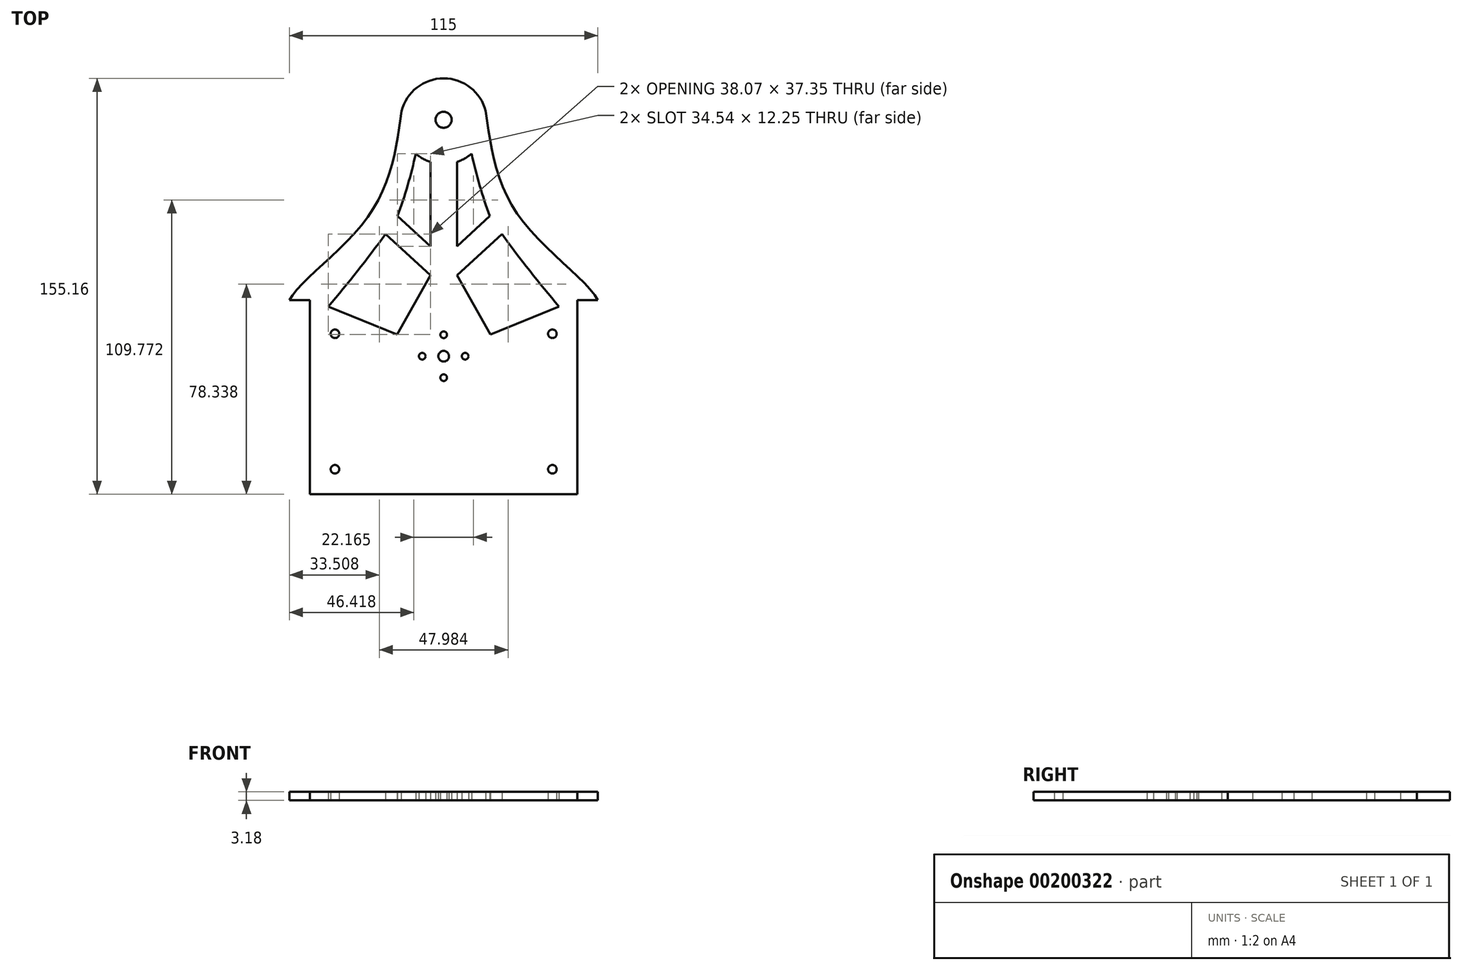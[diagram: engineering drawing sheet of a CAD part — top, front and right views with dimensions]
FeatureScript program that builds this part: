
annotation { "Feature Type Name" : "Feature", "Feature Type Description" : "" }
export const myFeature = defineFeature(function(context is Context, id is Id, definition is map)
    precondition{}
    {
        {
            var Q0;
            Q0=qCreatedBy(makeId("Top.planeOp"),FACE);
            var sketch = newSketch(context, id + "F0", { "sketchPlane" : qUnion([Q0])});
            skPoint(sketch, "E0.middle", {"position": v(0, 0) * mm});
            skPoint(sketch, "E1.orphan", {"position": v(-101.6, 120.65) * mm});
            skPoint(sketch, "E2.orphan", {"position": v(101.6, 120.65) * mm});
            skPoint(sketch, "E3.middle", {"position": v(0, -44.45) * mm});
            skPoint(sketch, "E4.middle", {"position": v(-64.58, -39.48) * mm});
            skPoint(sketch, "E5.orphan", {"position": v(-88.9, 0) * mm});
            skLineSegment(sketch, "E6", {"start": v(-49.88, -63.5) * mm, "end": v(49.88, -63.5) * mm});
            skLineSegment(sketch, "E7", {"start": v(-57.5, 8.9) * mm, "end": v(-49.88, 8.9) * mm});
            skLineSegment(sketch, "E8", {"start": v(-49.88, 8.9) * mm, "end": v(-49.88, -63.5) * mm});
            skPoint(sketch, "E9.orphan", {"position": v(-51.88, -63.5) * mm});
            skLineSegment(sketch, "E10.MirrorCS", {"start": v(49.88, 8.9) * mm, "end": v(49.88, -63.5) * mm});
            skLineSegment(sketch, "E11.MirrorCS", {"start": v(57.5, 8.9) * mm, "end": v(49.88, 8.9) * mm});
            skLineSegment(sketch, "E12.bottom", {"start": v(-50.88, 5.52) * mm, "end": v(-69.93, 5.52) * mm, "construction": true});
            skLineSegment(sketch, "E12.top", {"start": v(-50.88, -57.98) * mm, "end": v(-69.93, -57.98) * mm, "construction": true});
            skLineSegment(sketch, "E12.left", {"start": v(-50.88, 5.52) * mm, "end": v(-50.88, -57.98) * mm, "construction": true});
            skLineSegment(sketch, "E12.right", {"start": v(-69.93, 5.52) * mm, "end": v(-69.93, -57.98) * mm, "construction": true});
            skLineSegment(sketch, "E13.MirrorCS", {"start": v(50.88, 5.52) * mm, "end": v(69.93, 5.52) * mm, "construction": true});
            skLineSegment(sketch, "E14.MirrorCS", {"start": v(50.88, 5.52) * mm, "end": v(50.88, -57.98) * mm, "construction": true});
            skLineSegment(sketch, "E15.MirrorCS", {"start": v(50.88, -57.98) * mm, "end": v(69.93, -57.98) * mm, "construction": true});
            skLineSegment(sketch, "E16.MirrorCS", {"start": v(69.93, 5.52) * mm, "end": v(69.93, -57.98) * mm, "construction": true});
            skCircle(sketch, "E17", {"center": v(-0.03, 76.2) * mm, "radius": 3 * mm});
            skCircle(sketch, "E18", {"center": v(-0.03, 76.2) * mm, "radius": 63.5 * mm, "construction": true});
            skFitSpline(sketch, "E19", {"points": [v(-15.7, 79.38) * mm, v(-28.38, 39.82) * mm, v(-57.5, 8.9) * mm, v(-57.5, 1.27) * mm], "startDerivative": vector(-13.48, -99.48) * mm, "endDerivative": vector(13.07, -39.2) * mm});
            skFitSpline(sketch, "E20.MirrorCS", {"points": [v(15.7, 79.38) * mm, v(28.38, 39.82) * mm, v(57.5, 8.9) * mm, v(57.5, 1.27) * mm], "startDerivative": vector(13.48, -99.48) * mm, "endDerivative": vector(-13.07, -39.2) * mm});
            skArc(sketch, "E21", {"start": v(15.7, 79.38) * mm, "mid": v(0, 91.66) * mm, "end": v(-15.7, 79.38) * mm});
            skArc(sketch, "E22", {"start": v(-15.7, 79.38) * mm, "mid": v(-15.96, 78) * mm, "end": v(-16.09, 76.6) * mm});
            skLineSegment(sketch, "E23", {"start": v(-4.96, 60.5) * mm, "end": v(-4.96, 29) * mm});
            skLineSegment(sketch, "E24", {"start": v(-4.96, 29) * mm, "end": v(-17.2, 40.24) * mm});
            skArc(sketch, "E25", {"start": v(-17.2, 40.24) * mm, "mid": v(-13.4, 51.77) * mm, "end": v(-10.42, 63.54) * mm});
            skLineSegment(sketch, "E26", {"start": v(-4.96, 18.14) * mm, "end": v(-17.38, -3.84) * mm});
            skLineSegment(sketch, "E27", {"start": v(-17.38, -3.84) * mm, "end": v(-43.03, 6.52) * mm});
            skLineSegment(sketch, "E28", {"start": v(-4.96, 18.14) * mm, "end": v(-21.7, 33.51) * mm});
            skArc(sketch, "E29", {"start": v(-43.03, 6.52) * mm, "mid": v(-32.1, 19.81) * mm, "end": v(-21.7, 33.51) * mm});
            skLineSegment(sketch, "E30.MirrorCS", {"start": v(4.96, 18.14) * mm, "end": v(17.38, -3.84) * mm});
            skLineSegment(sketch, "E31.MirrorCS", {"start": v(4.96, 18.14) * mm, "end": v(21.7, 33.51) * mm});
            skLineSegment(sketch, "E32.MirrorCS", {"start": v(4.96, 29) * mm, "end": v(17.2, 40.24) * mm});
            skArc(sketch, "E33.MirrorCS", {"start": v(17.2, 40.24) * mm, "mid": v(13.4, 51.77) * mm, "end": v(10.42, 63.54) * mm});
            skLineSegment(sketch, "E34.MirrorCS", {"start": v(4.96, 60.5) * mm, "end": v(4.96, 29) * mm});
            skArc(sketch, "E35.MirrorCS", {"start": v(43.03, 6.52) * mm, "mid": v(32.1, 19.81) * mm, "end": v(21.7, 33.51) * mm});
            skLineSegment(sketch, "E36.MirrorCS", {"start": v(17.38, -3.84) * mm, "end": v(43.03, 6.52) * mm});
            skArc(sketch, "E37.trimOffspring", {"start": v(4.96, 60.5) * mm, "mid": v(7.84, 61.75) * mm, "end": v(10.42, 63.54) * mm});
            skLineSegment(sketch, "E38.trimOffspring", {"start": v(15.7, 79.38) * mm, "end": v(15.7, 79.38) * mm});
            skArc(sketch, "E39.trimOffspring", {"start": v(-10.42, 63.54) * mm, "mid": v(-7.84, 61.75) * mm, "end": v(-4.96, 60.5) * mm});
            skLineSegment(sketch, "E40.bottom", {"start": v(-49.88, -63.5) * mm, "end": v(-40.53, -63.5) * mm, "construction": true});
            skLineSegment(sketch, "E40.top", {"start": v(-49.88, -54.15) * mm, "end": v(-40.53, -54.15) * mm, "construction": true});
            skLineSegment(sketch, "E40.left", {"start": v(-49.88, -63.5) * mm, "end": v(-49.88, -54.15) * mm, "construction": true});
            skLineSegment(sketch, "E40.right", {"start": v(-40.53, -63.5) * mm, "end": v(-40.53, -54.15) * mm, "construction": true});
            skCircle(sketch, "E41", {"center": v(-40.53, -54.15) * mm, "radius": 1.6 * mm});
            skLineSegment(sketch, "E42.bottom", {"start": v(-49.88, 8.9) * mm, "end": v(-40.53, 8.9) * mm, "construction": true});
            skLineSegment(sketch, "E42.top", {"start": v(-49.88, -3.63) * mm, "end": v(-40.53, -3.63) * mm, "construction": true});
            skLineSegment(sketch, "E42.left", {"start": v(-49.88, 8.9) * mm, "end": v(-49.88, -3.63) * mm, "construction": true});
            skLineSegment(sketch, "E42.right", {"start": v(-40.53, 8.9) * mm, "end": v(-40.53, -3.63) * mm, "construction": true});
            skCircle(sketch, "E43", {"center": v(-40.53, -3.63) * mm, "radius": 1.6 * mm});
            skCircle(sketch, "E44.MirrorC", {"center": v(40.53, -3.63) * mm, "radius": 1.6 * mm});
            skCircle(sketch, "E45.MirrorC", {"center": v(40.53, -54.15) * mm, "radius": 1.6 * mm});
            skCircle(sketch, "E46", {"center": v(0, -12) * mm, "radius": 13.5 * mm, "construction": true});
            skCircle(sketch, "E47", {"center": v(0, -12) * mm, "radius": 2 * mm});
            skCircle(sketch, "E48", {"center": v(0, -4) * mm, "radius": 1.25 * mm});
            skLineSegment(sketch, "E49", {"start": v(-13.5, -12) * mm, "end": v(13.5, -12) * mm, "construction": true});
            skCircle(sketch, "E50.1.0", {"center": v(-8, -12) * mm, "radius": 1.25 * mm});
            skCircle(sketch, "E50.2.0", {"center": v(0, -20) * mm, "radius": 1.25 * mm});
            skCircle(sketch, "E50.3.0", {"center": v(8, -12) * mm, "radius": 1.25 * mm});
            skSolve(sketch);
        }
        {
            var Q0;
            Q0=makeQuery(id+"F0.imprint","IMPRINT",FACE,{"disambiguationData":[TD([[makeQuery(id+"F0.imprint","IMPRINT",EDGE,{"derivedFrom":sQuery(id+"F0.wireOp",EDGE,"XoACZhgm-4fXt-D90R-Zf98-5iFfzIu4IJjn")}),1.0]])]});
            var Q1;
            Q1=makeQuery(id+"F0.imprint","IMPRINT",FACE,{"disambiguationData":[TD([[makeQuery(id+"F0.imprint","IMPRINT",EDGE,{"derivedFrom":sQuery(id+"F0.wireOp",EDGE,"E3.bottom")}),1.0]])]});
            var Q2;
            {var subQ3=sQuery(id+"F0.wireOp",EDGE,"6qRwDFxo-6jyo-wpqG-2Wls-fq8RWR64ATTu");Q2=makeQuery(id+"F0.imprint","IMPRINT",FACE,{"disambiguationData":[TD([[makeQuery(id+"F0.imprint","IMPRINT",EDGE,{"derivedFrom":subQ3}),-1.0]])]});}
            var Q3;
            Q3=makeQuery(id+"F0.imprint","IMPRINT",FACE,{"disambiguationData":[TD([[makeQuery(id+"F0.imprint","IMPRINT",EDGE,{"derivedFrom":sQuery(id+"F0.wireOp",EDGE,"E6")}),1.0]])]});
            extrude(context, id + "F1", {"entities" : qUnion([Q0, Q1, Q2, Q3]), "depth" : 3.17 * mm});
        }
    });
